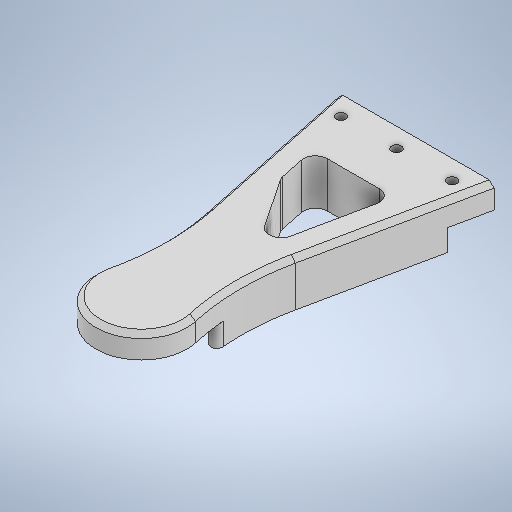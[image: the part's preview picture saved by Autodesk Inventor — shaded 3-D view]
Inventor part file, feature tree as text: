
AUTODESK INVENTOR PART (.ipt)
format: ipt  version: 2025.2 (Build 292293000, 293)  size: 643,584 bytes
history: native  units: mm
features: extrude x12, sketch x12, other x8, reference x7, projected_geometry x4, chamfer x2, fillet x1, mirror x1
ambient origin geometry x8: Origin, YZ Plane, XZ Plane, XY Plane, X Axis, Y Axis, Z Axis, Center Point
bodies: Solid1 (feature_tree)
feature tree (47):
  extrude  "Extrusion1"  Depth=75.0mm
  extrude  "Extrusion4"  Depth=47.0mm
  extrude  "Extrusion5"  Depth=4.0mm
  extrude  "Extrusion6"  Depth=16.256841mm
  extrude  "Extrusion7"  Depth=35.0mm
  extrude  "Extrusion8"  Depth=48.150251mm
  extrude  "Extrusion11"  Depth=48.150251mm
  chamfer  "Chamfer1"  Distance=8.128925mm
  extrude  "Extrusion16"  Depth=2.0mm
  extrude  "Extrusion17"  TaperAngle=0.0deg  [1 undecoded]
  extrude  "Extrusion18"  Depth=16.256841mm
  extrude  "Extrusion19"  Depth=2.0mm
  fillet  "Fillet2"  Radius=16.256841mm
  mirror  "Mirror1"
  extrude  "Extrusion20"  Depth=10.0mm TaperAngle=0.0deg
  chamfer  "Chamfer2"  [1 undecoded]
  sketch  "Sketch1"  dims[d0=150.0mm d1=75.0mm]
  sketch  "Sketch4"  dims[d22=38.0mm d33=47.0mm]
  reference  "Reference1"
  sketch  "Sketch5"  dims[d34=4.0mm d35=12.533523mm]
  sketch  "Sketch6"  dims[d36=12.533523mm d37=16.256841mm]
  sketch  "Sketch7"  dims[d38=35.0mm d39=35.0mm]
  reference  "Reference2"
  sketch  "Sketch8"  dims[d40=0.0mm d41=48.150251mm]
  sketch  "Sketch11"  dims[d42=0.0mm d43=48.150251mm]
  reference  "Reference4"
  reference  "Reference5"
  sketch  "Sketch17"  dims[d44=0.0mm]
  reference  "Reference9"
  reference  "Reference10"
  projected_geometry  "Projected Loop2"
  sketch  "Sketch18"  dims[d45=8.128925mm]
  reference  "Reference11"
  projected_geometry  "Projected Loop3"
  sketch  "Sketch19"  dims[d46=10.137333mm]
  sketch  "Sketch20"  dims[d47=8.128925mm]
  projected_geometry  "Projected Loop4"
  sketch  "Sketch21"  dims[d48=21.537769mm d49=8.128925mm d50=32.938205mm d51=0.0mm d52=16.256841mm d53=38.001454mm d54=16.256841mm d55=10.0mm d56=0.0mm d67=0.0mm d68=0.0mm d69=4.45mm d70=4.45mm d71=4.45mm d72=6.0mm d73=0.0mm d74=6.0mm d75=0.0mm d76=10.0mm d77=0.0mm d80=100.0mm d81=10.0mm d82=0.0mm d93=0.0mm d94=0.0mm d95=2.0mm d96=2.0mm d97=45.0deg d113=9.0mm d114=0.0mm d117=7.05mm d118=9.0mm d119=0.0mm d120=4.45mm d121=7.05mm d122=4.45mm d123=9.5mm d124=0.0mm d125=10.0mm d126=10.0mm d127=0.0mm d128=5.0mm d129=17.0mm d130=0.85mm d131=0.2mm d132=0.0mm d133=0.2mm d134=2.0mm d135=45.0deg]
  projected_geometry  "Projected Loop5"
  parser-record x2  (decoder bookkeeping rows leaked as tree rows — omitted from the tree; the rows remain in map.json)
  other  "leg_articulation_assembly.iam"
  other  "motion_thigh_top:1"
  other  "Big_drum:1"
  other  "WBR.iam"
  other  "leg_wheel:1"
  other  "leg_extend:1"
note: 2 required parameter values undecoded (feature->parameter linkage not recoverable at this tier; creation-order binding heuristic only, values carry confidence <= 0.55)
note: 2 file-system paths scrubbed to <path> (originals preserved in map.json)
